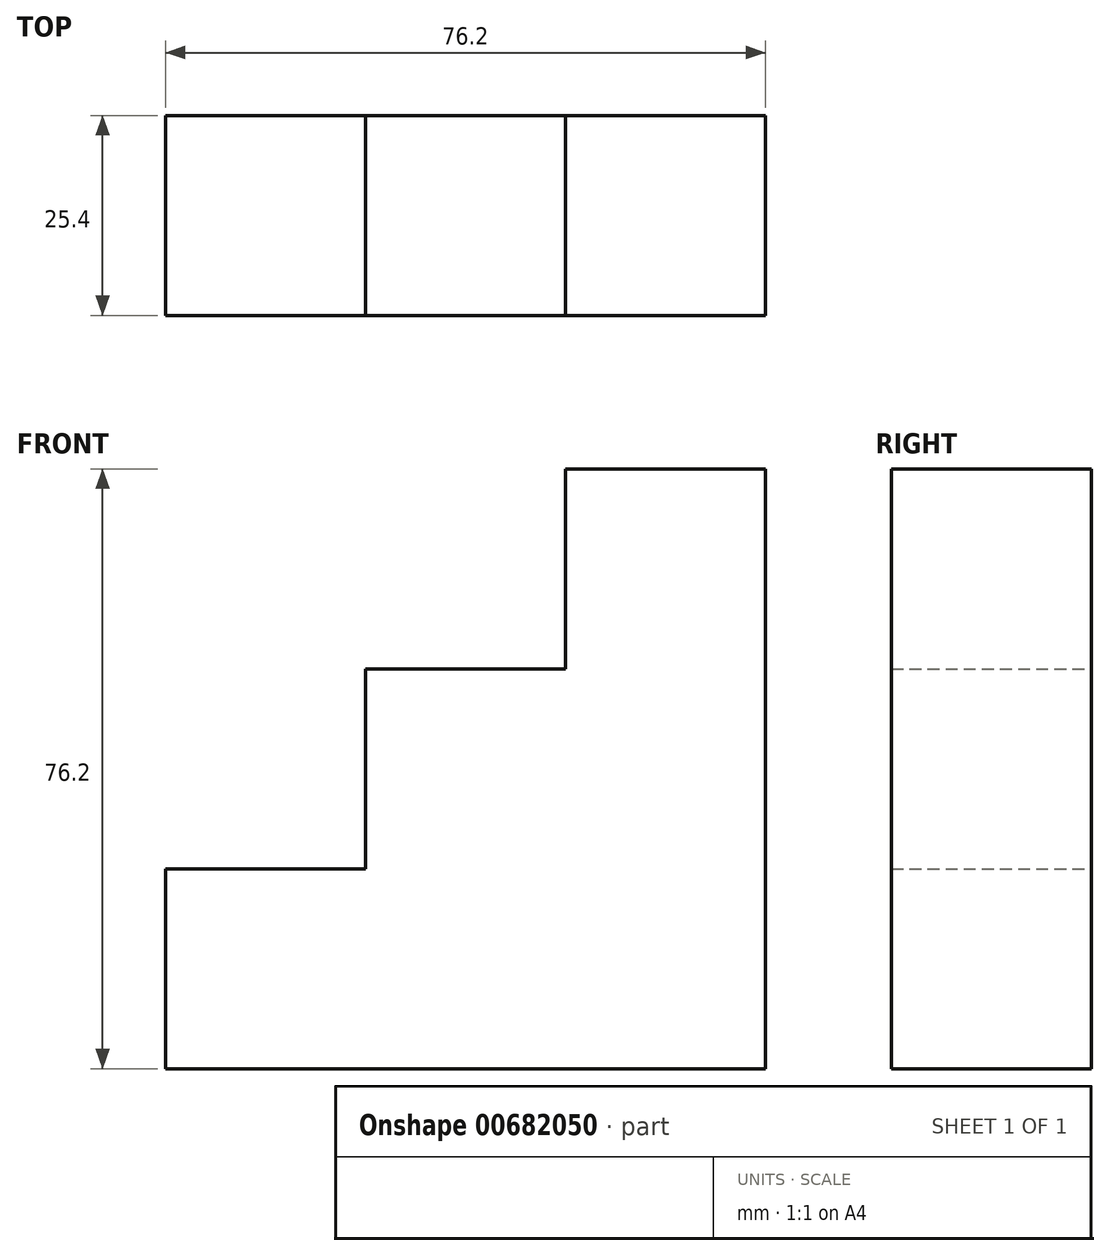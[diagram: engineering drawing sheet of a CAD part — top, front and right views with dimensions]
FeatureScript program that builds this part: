
annotation { "Feature Type Name" : "Feature", "Feature Type Description" : "" }
export const myFeature = defineFeature(function(context is Context, id is Id, definition is map)
    precondition{}
    {
        {
            var Q0;
            Q0=qCreatedBy(makeId("Front.planeOp"),FACE);
            var sketch = newSketch(context, id + "F0", { "sketchPlane" : qUnion([Q0])});
            skLineSegment(sketch, "E0", {"start": v(0, 0) * mm, "end": v(76.2, 0) * mm});
            skLineSegment(sketch, "E1", {"start": v(76.2, 0) * mm, "end": v(76.2, 76.2) * mm});
            skLineSegment(sketch, "E2", {"start": v(76.2, 76.2) * mm, "end": v(50.8, 76.2) * mm});
            skLineSegment(sketch, "E3", {"start": v(50.8, 76.2) * mm, "end": v(50.8, 50.8) * mm});
            skLineSegment(sketch, "E4", {"start": v(50.8, 50.8) * mm, "end": v(25.4, 50.8) * mm});
            skLineSegment(sketch, "E5", {"start": v(25.4, 50.8) * mm, "end": v(25.4, 25.4) * mm});
            skLineSegment(sketch, "E6", {"start": v(25.4, 25.4) * mm, "end": v(0, 25.4) * mm});
            skLineSegment(sketch, "E7", {"start": v(0, 25.4) * mm, "end": v(0, 0) * mm});
            skSolve(sketch);
        }
        {
            var Q0;
            Q0 = qSketchRegion(id + "F0", true);
            extrude(context, id + "F1", {"entities" : qUnion([Q0]), "depth" : 25.4 * mm, "offsetDistance" : 25.4 * mm});
        }
    });
